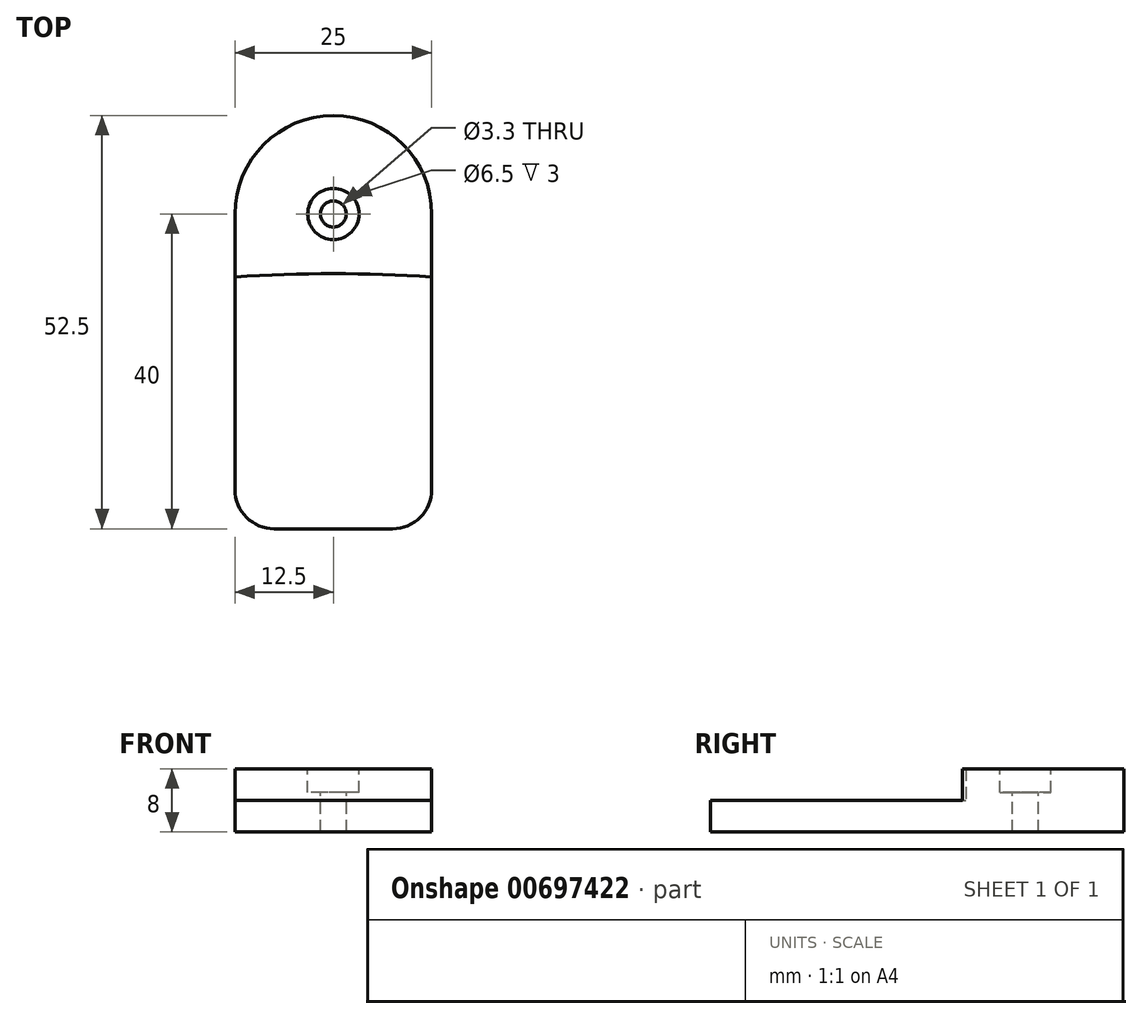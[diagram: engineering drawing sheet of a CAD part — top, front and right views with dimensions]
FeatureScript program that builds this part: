
annotation { "Feature Type Name" : "Feature", "Feature Type Description" : "" }
export const myFeature = defineFeature(function(context is Context, id is Id, definition is map)
    precondition{}
    {
        {
            var Q0;
            Q0=qCreatedBy(makeId("Top.planeOp"),FACE);
            var sketch = newSketch(context, id + "F0", { "sketchPlane" : qUnion([Q0])});
            skLineSegment(sketch, "E0", {"start": v(0, 5) * mm, "end": v(0, 40) * mm});
            skLineSegment(sketch, "E1", {"start": v(25, 40) * mm, "end": v(25, 5) * mm});
            skLineSegment(sketch, "E2", {"start": v(20, 0) * mm, "end": v(5, 0) * mm});
            skArc(sketch, "E3", {"start": v(25, 40) * mm, "mid": v(12.5, 52.5) * mm, "end": v(0, 40) * mm});
            skArc(sketch, "E4", {"start": v(25, 32) * mm, "mid": v(12.5, 32.41) * mm, "end": v(0, 32) * mm});
            skPoint(sketch, "E5.visualSharp", {"position": v(0, 0) * mm});
            skArc(sketch, "E5.filletArc", {"start": v(0, 5) * mm, "mid": v(1.46, 1.46) * mm, "end": v(5, 0) * mm});
            skPoint(sketch, "E6.visualSharp", {"position": v(25, 0) * mm});
            skArc(sketch, "E6.filletArc", {"start": v(20, 0) * mm, "mid": v(23.54, 1.46) * mm, "end": v(25, 5) * mm});
            skSolve(sketch);
        }
        {
            var Q0;
            {var subQ0=sQuery(id+"F0.wireOp",EDGE,"E3");Q0=makeQuery(id+"F0.imprint","IMPRINT",FACE,{"disambiguationData":[TD([[makeQuery(id+"F0.imprint","IMPRINT",EDGE,{"derivedFrom":subQ0}),1.0]])]});}
            extrude(context, id + "F1", {"entities" : qUnion([Q0]), "depth" : 8 * mm, "offsetDistance" : 25 * mm});
        }
        {
            var Q0;
            Q0=makeQuery(id+"F0.imprint","IMPRINT",FACE,{"disambiguationData":[TD([[makeQuery(id+"F0.imprint","IMPRINT",EDGE,{"derivedFrom":sQuery(id+"F0.wireOp",EDGE,"E2")}),-1.0]])]});
            extrude(context, id + "F2", {"entities" : qUnion([Q0]), "operationType" : NewBodyOperationType.ADD, "depth" : 4 * mm, "offsetDistance" : 25 * mm});
        }
        {
            var Q0;
            Q0=makeQuery(id+"F1.opExtrude","CAP_FACE",FACE,{"disambiguationData":[OSD([sQuery(id+"F0.wireOp",EDGE,"E0"),sQuery(id+"F0.wireOp",EDGE,"E1"),sQuery(id+"F0.wireOp",EDGE,"E3"),sQuery(id+"F0.wireOp",EDGE,"E4")])],"isStart":false});
            var sketch = newSketch(context, id + "F3", { "sketchPlane" : qUnion([Q0])});
            skPoint(sketch, "E7", {"position": v(12.5, 40) * mm});
            skSolve(sketch);
        }
        {
            var Q0;
            Q0=sQuery(id+"F3.wireOp",VERTEX,"E7");
            var Q1;
            Q1=makeQuery(id+"F1.opExtrude","SWEPT_BODY",BODY,{"disambiguationData":[OSD([sQuery(id+"F0.wireOp",EDGE,"E0"),sQuery(id+"F0.wireOp",EDGE,"E1"),sQuery(id+"F0.wireOp",EDGE,"E3"),sQuery(id+"F0.wireOp",EDGE,"E4")])]});
            hole(context, id + "F4", {"style" : HoleStyle.C_BORE, "endStyle" : HoleEndStyle.THROUGH, "standardTappedOrClearance" : lookupTablePath({ "standard" : "ISO", "fit" : "Normal", "size" : "M3", "type" : "Clearance" }), "standardBlindInLast" : lookupTablePath({ "fit" : "Standard", "standard" : "ISO", "size" : "M3", "type" : "Clearance" }), "holeDiameter" : 3.3 * mm, "cBoreDiameter" : 6.5 * mm, "cBoreDepth" : 3 * mm, "majorDiameter" : 5 * mm, "isTappedThrough" : true, "tappedDepth" : 12 * mm, "tapClearance" : 3, "locations" : qUnion([Q0]), "scope" : qUnion([Q1])});
        }
    });
